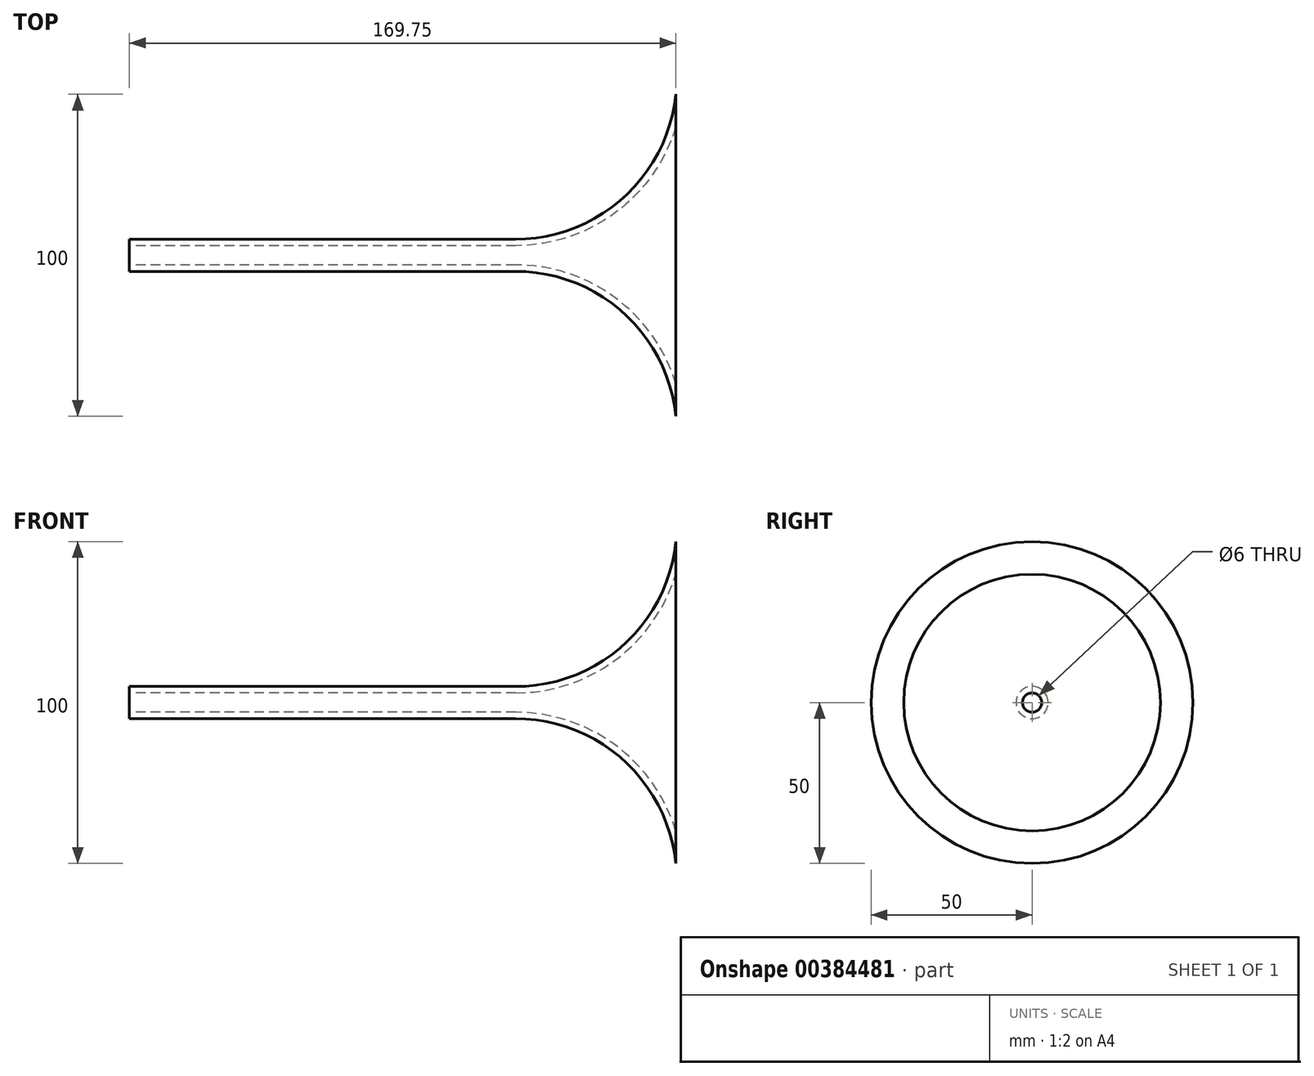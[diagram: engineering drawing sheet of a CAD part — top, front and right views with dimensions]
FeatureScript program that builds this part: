
annotation { "Feature Type Name" : "Feature", "Feature Type Description" : "" }
export const myFeature = defineFeature(function(context is Context, id is Id, definition is map)
    precondition{}
    {
        {
            var Q0;
            Q0=qCreatedBy(makeId("Top.planeOp"),FACE);
            var sketch = newSketch(context, id + "F0", { "sketchPlane" : qUnion([Q0])});
            skPoint(sketch, "E0.start.orphan", {"position": v(-83.96, 0) * mm});
            skLineSegment(sketch, "E1", {"start": v(-48, 5) * mm, "end": v(72, 5) * mm});
            skArc(sketch, "E2", {"start": v(72, 5) * mm, "mid": v(105.54, 17.92) * mm, "end": v(121.75, 50) * mm});
            skLineSegment(sketch, "E3", {"start": v(-83.96, 0) * mm, "end": v(93.72, 0) * mm, "construction": true});
            skLineSegment(sketch, "E4.0", {"start": v(-48, 3) * mm, "end": v(72, 3) * mm});
            skArc(sketch, "E5.0", {"start": v(72, 3) * mm, "mid": v(102.96, 13.22) * mm, "end": v(121.75, 39.87) * mm});
            skLineSegment(sketch, "E6", {"start": v(-48, 5) * mm, "end": v(-48, 3) * mm});
            skLineSegment(sketch, "E7", {"start": v(121.75, 50) * mm, "end": v(121.75, 39.87) * mm});
            skSolve(sketch);
        }
        {
            var Q0;
            Q0=makeQuery(id+"F0.imprint","IMPRINT",FACE,{"disambiguationData":[TD([[makeQuery(id+"F0.imprint","IMPRINT",EDGE,{"derivedFrom":sQuery(id+"F0.wireOp",EDGE,"E1")}),-1.0]])]});
            var Q1;
            Q1=sQuery(id+"F0.wireOp",EDGE,"E3");
            revolve(context, id + "F1", {"entities" : qUnion([Q0]), "axis" : qUnion([Q1]), "revolveType" : RevolveType.FULL});
        }
    });
